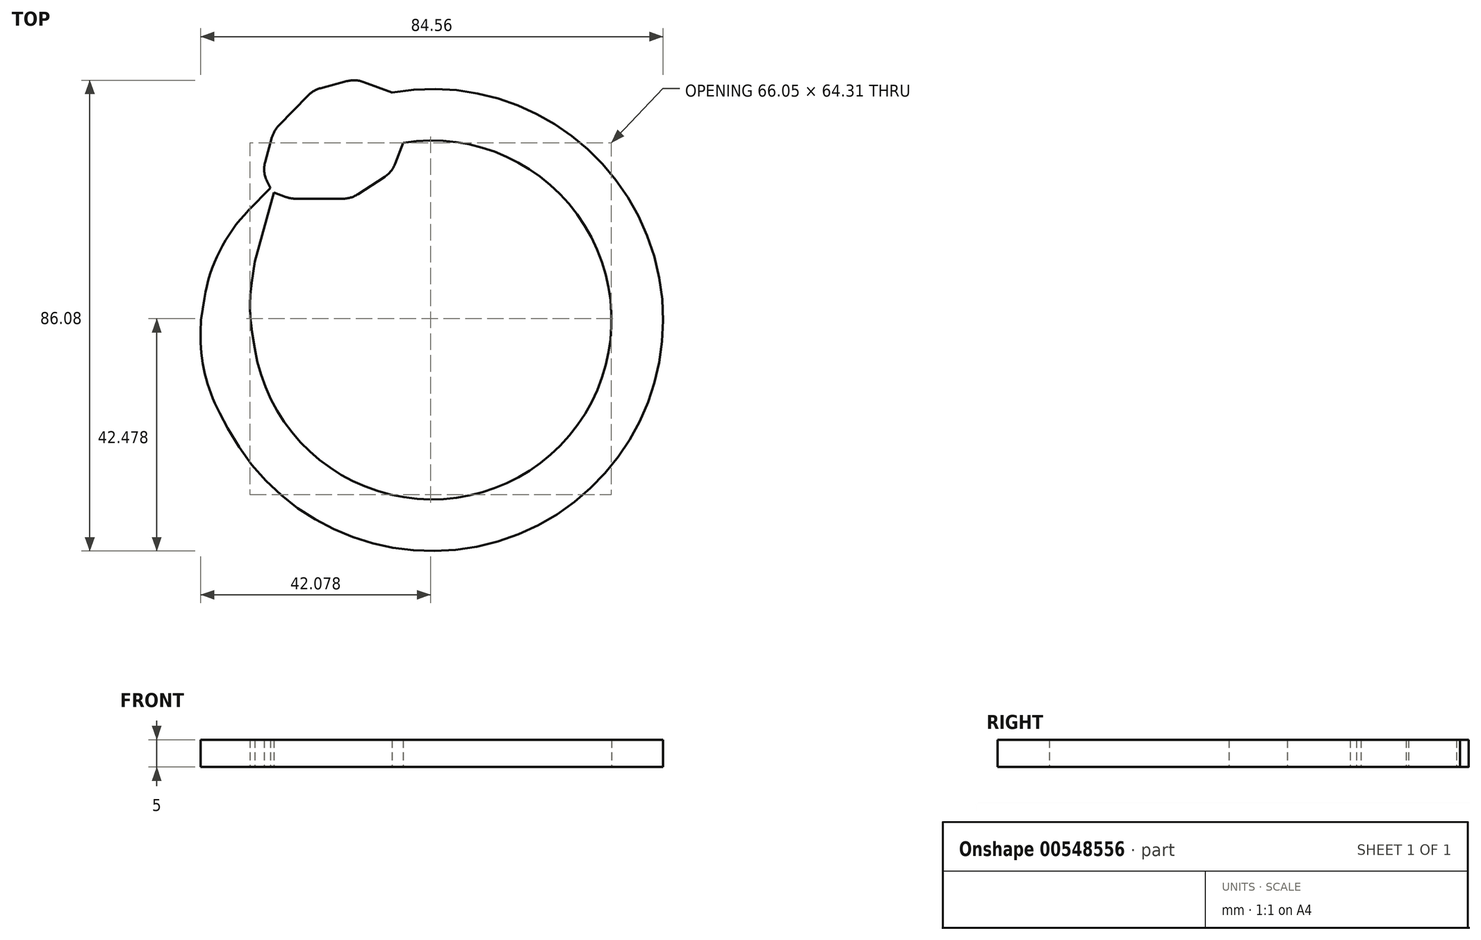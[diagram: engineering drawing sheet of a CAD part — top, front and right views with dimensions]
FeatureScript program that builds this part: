
annotation { "Feature Type Name" : "Feature", "Feature Type Description" : "" }
export const myFeature = defineFeature(function(context is Context, id is Id, definition is map)
    precondition{}
    {
        {
            var Q0;
            Q0=qCreatedBy(makeId("Top.planeOp"),FACE);
            var sketch = newSketch(context, id + "F0", { "sketchPlane" : qUnion([Q0])});
            skArc(sketch, "E0", {"start": v(-37.31, -19.81) * mm, "mid": v(37.96, -18.55) * mm, "end": v(-7.29, 41.62) * mm});
            skArc(sketch, "E1", {"start": v(-32.4, -5.2) * mm, "mid": v(26.61, -19.2) * mm, "end": v(-5.28, 32.38) * mm});
            skLineSegment(sketch, "E2", {"start": v(-32.4, -5.2) * mm, "end": v(-32.4, 10.65) * mm});
            skLineSegment(sketch, "E3", {"start": v(-40.12, 13.25) * mm, "end": v(-42.25, 0) * mm});
            skLineSegment(sketch, "E4", {"start": v(-40.12, 13.25) * mm, "end": v(-29.55, 24.14) * mm});
            skLineSegment(sketch, "E5", {"start": v(-28.9, 23.33) * mm, "end": v(-32.4, 10.65) * mm});
            skLineSegment(sketch, "E6", {"start": v(-29.55, 24.14) * mm, "end": v(-30.98, 27.07) * mm});
            skLineSegment(sketch, "E7", {"start": v(-30.98, 27.07) * mm, "end": v(-28.9, 34.61) * mm});
            skLineSegment(sketch, "E8", {"start": v(-28.9, 34.61) * mm, "end": v(-21.72, 42.02) * mm});
            skLineSegment(sketch, "E9", {"start": v(-21.72, 42.02) * mm, "end": v(-14, 44.06) * mm});
            skLineSegment(sketch, "E10", {"start": v(-14, 44.06) * mm, "end": v(-7.29, 41.62) * mm});
            skLineSegment(sketch, "E11", {"start": v(-5.28, 32.38) * mm, "end": v(-7.29, 27.07) * mm});
            skLineSegment(sketch, "E12", {"start": v(-7.29, 27.07) * mm, "end": v(-14.78, 22.18) * mm});
            skLineSegment(sketch, "E13", {"start": v(-14.78, 22.18) * mm, "end": v(-25.87, 22.18) * mm});
            skLineSegment(sketch, "E14", {"start": v(-25.87, 22.18) * mm, "end": v(-28.9, 23.33) * mm});
            skLineSegment(sketch, "E15", {"start": v(-37.31, -19.81) * mm, "end": v(-42.5, -10.05) * mm});
            skLineSegment(sketch, "E16", {"start": v(-42.5, -10.05) * mm, "end": v(-42.25, 0) * mm});
            skSolve(sketch);
        }
        {
            var Q0;
            Q0=makeQuery(id+"F0.imprint","IMPRINT",FACE,{"disambiguationData":[TD([[makeQuery(id+"F0.imprint","IMPRINT",EDGE,{"derivedFrom":sQuery(id+"F0.wireOp",EDGE,"E0")}),1.0]])]});
            extrude(context, id + "F1", {"entities" : qUnion([Q0]), "depth" : 5 * mm, "offsetDistance" : 25 * mm});
        }
        {
            var Q0;
            Q0=makeQuery(id+"F1.opExtrude","SWEPT_EDGE",EDGE,{"disambiguationData":[OSD([sQuery(id+"F0.wireOp",EDGE,"E15"),sQuery(id+"F0.wireOp",EDGE,"E16")])]});
            fillet(context, id + "F2", {"entities" : qUnion([Q0]), "radius" : 30 * mm, "tangentPropagation" : true, "allowEdgeOverflow" : false});
        }
        {
            var Q0;
            Q0=makeQuery(id+"F1.opExtrude","CAP_FACE",FACE,{"disambiguationData":[OSD([sQuery(id+"F0.wireOp",EDGE,"E0"),sQuery(id+"F0.wireOp",EDGE,"E1"),sQuery(id+"F0.wireOp",EDGE,"E2"),sQuery(id+"F0.wireOp",EDGE,"E3"),sQuery(id+"F0.wireOp",EDGE,"E4"),sQuery(id+"F0.wireOp",EDGE,"E5"),sQuery(id+"F0.wireOp",EDGE,"E6"),sQuery(id+"F0.wireOp",EDGE,"E7"),sQuery(id+"F0.wireOp",EDGE,"E8"),sQuery(id+"F0.wireOp",EDGE,"E9"),sQuery(id+"F0.wireOp",EDGE,"E10"),sQuery(id+"F0.wireOp",EDGE,"E11"),sQuery(id+"F0.wireOp",EDGE,"E12"),sQuery(id+"F0.wireOp",EDGE,"E13"),sQuery(id+"F0.wireOp",EDGE,"E14"),sQuery(id+"F0.wireOp",EDGE,"E15"),sQuery(id+"F0.wireOp",EDGE,"E16")])],"isStart":false});
            var sketch = newSketch(context, id + "F3", { "sketchPlane" : qUnion([Q0])});
            skLineSegment(sketch, "E17", {"start": v(-32.4, -5.2) * mm, "end": v(-33.6, 2.29) * mm});
            skLineSegment(sketch, "E18", {"start": v(-33.6, 2.29) * mm, "end": v(-32.4, 10.65) * mm});
            skLineSegment(sketch, "E19", {"start": v(-32.4, 10.65) * mm, "end": v(-32.4, -5.2) * mm});
            skSolve(sketch);
        }
        {
            var Q0;
            Q0 = qSketchRegion(id + "F3", true);
            extrude(context, id + "F4", {"entities" : qUnion([Q0]), "operationType" : NewBodyOperationType.REMOVE, "endBound" : BoundingType.THROUGH_ALL, "oppositeDirection" : true, "depth" : 5 * mm, "offsetDistance" : 25 * mm});
        }
        {
            var Q0;
            Q0=makeQuery(id+"F1.opExtrude","SWEPT_EDGE",EDGE,{"disambiguationData":[OSD([sQuery(id+"F0.wireOp",EDGE,"E3"),sQuery(id+"F0.wireOp",EDGE,"E4")])]});
            fillet(context, id + "F5", {"entities" : qUnion([Q0]), "radius" : 30 * mm, "tangentPropagation" : true, "allowEdgeOverflow" : false});
        }
        {
            var Q0;
            Q0=makeQuery(id+"F4.boolean.opBoolean","COPY",EDGE,{"derivedFrom":makeQuery(id+"F4.opExtrude","SWEPT_EDGE",EDGE,{"disambiguationData":[OSD([sQuery(id+"F3.wireOp",EDGE,"E17"),sQuery(id+"F3.wireOp",EDGE,"E18")])]})});
            fillet(context, id + "F6", {"entities" : qUnion([Q0]), "radius" : 30 * mm, "tangentPropagation" : true, "allowEdgeOverflow" : false});
        }
        {
            var Q0;
            Q0=makeQuery(id+"F1.opExtrude","SWEPT_EDGE",EDGE,{"disambiguationData":[OSD([sQuery(id+"F0.wireOp",EDGE,"E6"),sQuery(id+"F0.wireOp",EDGE,"E7")])]});
            fillet(context, id + "F7", {"entities" : qUnion([Q0]), "radius" : 5 * mm, "tangentPropagation" : true, "allowEdgeOverflow" : false});
        }
        {
            var Q0;
            Q0=makeQuery(id+"F1.opExtrude","SWEPT_EDGE",EDGE,{"disambiguationData":[OSD([sQuery(id+"F0.wireOp",EDGE,"E13"),sQuery(id+"F0.wireOp",EDGE,"E14")])]});
            fillet(context, id + "F8", {"entities" : qUnion([Q0]), "radius" : 5 * mm, "tangentPropagation" : true, "allowEdgeOverflow" : false});
        }
        {
            var Q0;
            Q0=makeQuery(id+"F1.opExtrude","SWEPT_EDGE",EDGE,{"disambiguationData":[OSD([sQuery(id+"F0.wireOp",EDGE,"E7"),sQuery(id+"F0.wireOp",EDGE,"E8")])]});
            var Q1;
            Q1=makeQuery(id+"F1.opExtrude","SWEPT_EDGE",EDGE,{"disambiguationData":[OSD([sQuery(id+"F0.wireOp",EDGE,"E8"),sQuery(id+"F0.wireOp",EDGE,"E9")])]});
            var Q2;
            Q2=makeQuery(id+"F1.opExtrude","SWEPT_EDGE",EDGE,{"disambiguationData":[OSD([sQuery(id+"F0.wireOp",EDGE,"E9"),sQuery(id+"F0.wireOp",EDGE,"E10")])]});
            fillet(context, id + "F9", {"entities" : qUnion([Q0, Q1, Q2]), "radius" : 5 * mm, "tangentPropagation" : true, "allowEdgeOverflow" : false});
        }
        {
            var Q0;
            Q0=makeQuery(id+"F1.opExtrude","SWEPT_EDGE",EDGE,{"disambiguationData":[OSD([sQuery(id+"F0.wireOp",EDGE,"E12"),sQuery(id+"F0.wireOp",EDGE,"E13")])]});
            var Q1;
            Q1=makeQuery(id+"F1.opExtrude","SWEPT_EDGE",EDGE,{"disambiguationData":[OSD([sQuery(id+"F0.wireOp",EDGE,"E11"),sQuery(id+"F0.wireOp",EDGE,"E12")])]});
            fillet(context, id + "F10", {"entities" : qUnion([Q0, Q1]), "radius" : 5 * mm, "tangentPropagation" : true, "allowEdgeOverflow" : false});
        }
    });
